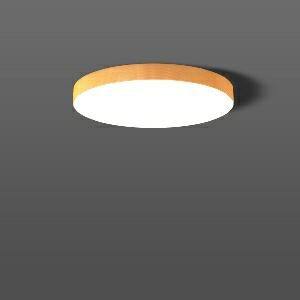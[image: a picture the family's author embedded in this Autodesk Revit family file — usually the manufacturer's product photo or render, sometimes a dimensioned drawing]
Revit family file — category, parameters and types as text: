
# Revit family: flatliner_slim_312287_002_76_7646
name_source: partatom
category: Lighting Fixtures
units: mm (PartAtom-declared; Revit-internal decimal feet)

## family parameters
Cut with Voids When Loaded = No
Host = Face
Light Source = No
Part Type = Normal
Room Calculation Point = No
Round Connector Dimension = Use Diameter
Shared = No

## types (1)
- 982559.002 (1 x LED Modul 830, 2750 lm, 3000)
    Apparent Load = 38 VA
    CIE Flux Codes = 45 76 94 95 100
    Color Rendering = 80
    Color Temperature = 3000
    Default Elevation = 1800 mm
    Description = Series: FLATLINER SLIM
Decorative ceiling luminaire for interior decoration. Base luminaire prepared for the installation of fabric lampshade. Base: metal, white, powder-coated. TouchDim sensor capable. Light and/or presence sensors can be integrated. Modular design: with the basic luminaire, a cylindrical fabric lampshade with a polycarbonate satin-finish diffuser must always be ordered separately. Fabric lampshade and diffuser can be assembled without the use of tools. 
Colour: white
Diameter: 596 mm
Height: 34 mm
Lamp: LED exchangeable
Socket: without socket
Colour temperature: 3000K
Colour rendering index (CRI): 83
System power: 38 W
Rated luminous flux: 2750 lm
Beam angle Down: 117°
Luminous efficiency: 72 lm/W
Control gear: AC power, DALI dimmable
Protection class: I
Type of protection: IP 20
    Height = 34 mm  [stored 0.111549 ft]
    Lamp = 1 x LED Modul 830
    Lamp Light Flux = 2750 lm
    Lamp count = 1
    Length = 596 mm
    Lifetime = 50000 h
    Luminous efficacy = 72 lm/W
    Manufacturer = RZB
    ModVariant = No
    Model = 312287.002.76
    Mounting Place = Ceiling
    Mounting Type = Surface mounted
    Number of Poles = 1
    OnlyDefault = Yes
    Power Factor = 1
    Product Name = FLATLINER SLIM
    Product group = Surface mounted ceiling Fabric lampshade luminaires
    ProductGroupID = 313
    Protection Class = Protection class I
    Protection Degree = IP 20
    RLX_Detail_Level = 1
    RLX_Emergency_Light_Flux = 0 lm
    RLX_Emergency_Type = 0
    RLX_Emergency_Type_DB = No
    RlxData = <blob elided: 23897 chars, md5=18dd059a>
    Socket = socket
    Standby Power = 0 W
    System Light Flux = 2750 lm
    System Power = 38 W
    Type Image = 312287.002_982442.0063_982444.002.jpg
    URL = http://relux.com
    VarID = 982559_002_a29f
    Voltage = 230 V
    Voltage Range = 220-240 V
    Weight = 0.00 kg
    Width = 0 mm  [stored 0 ft]

note: [stored X ft] marks values corroborated as IEEE doubles in the binary element streams (Revit-internal decimal feet)

## geometry (parser evidence)
native form markers: Blend x4, Sweep x13
no freeform markers — native parametric forms only
